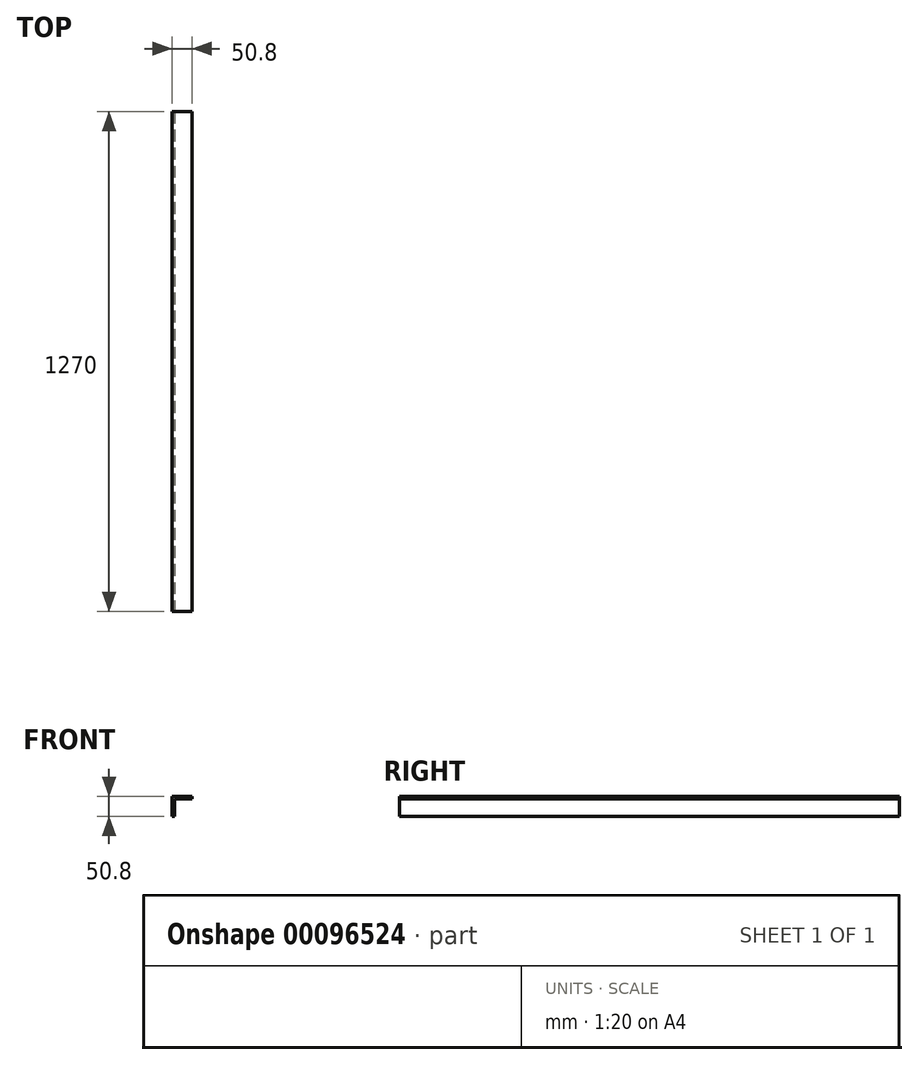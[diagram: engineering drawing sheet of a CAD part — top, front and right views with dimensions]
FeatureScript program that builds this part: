
annotation { "Feature Type Name" : "Feature", "Feature Type Description" : "" }
export const myFeature = defineFeature(function(context is Context, id is Id, definition is map)
    precondition{}
    {
        {
            var Q0;
            Q0=qCreatedBy(makeId("Front.planeOp"),FACE);
            var sketch = newSketch(context, id + "F0", { "sketchPlane" : qUnion([Q0])});
            skLineSegment(sketch, "E0", {"start": v(0, 0) * mm, "end": v(-50.8, 0) * mm});
            skLineSegment(sketch, "E1", {"start": v(-50.8, 0) * mm, "end": v(-50.8, -50.8) * mm});
            skLineSegment(sketch, "E2.0", {"start": v(-44.45, -6.35) * mm, "end": v(-44.45, -50.8) * mm});
            skLineSegment(sketch, "E2.1", {"start": v(0, -6.35) * mm, "end": v(-44.45, -6.35) * mm});
            skLineSegment(sketch, "E3", {"start": v(-50.8, -50.8) * mm, "end": v(-44.45, -50.8) * mm});
            skLineSegment(sketch, "E4", {"start": v(0, -6.35) * mm, "end": v(0, 0) * mm});
            skSolve(sketch);
        }
        {
            var Q0;
            Q0=qSketchRegion(id+"F0",true);
            extrude(context, id + "F1", {"entities" : qUnion([Q0]), "oppositeDirection" : true, "depth" : 1270 * mm});
        }
    });
